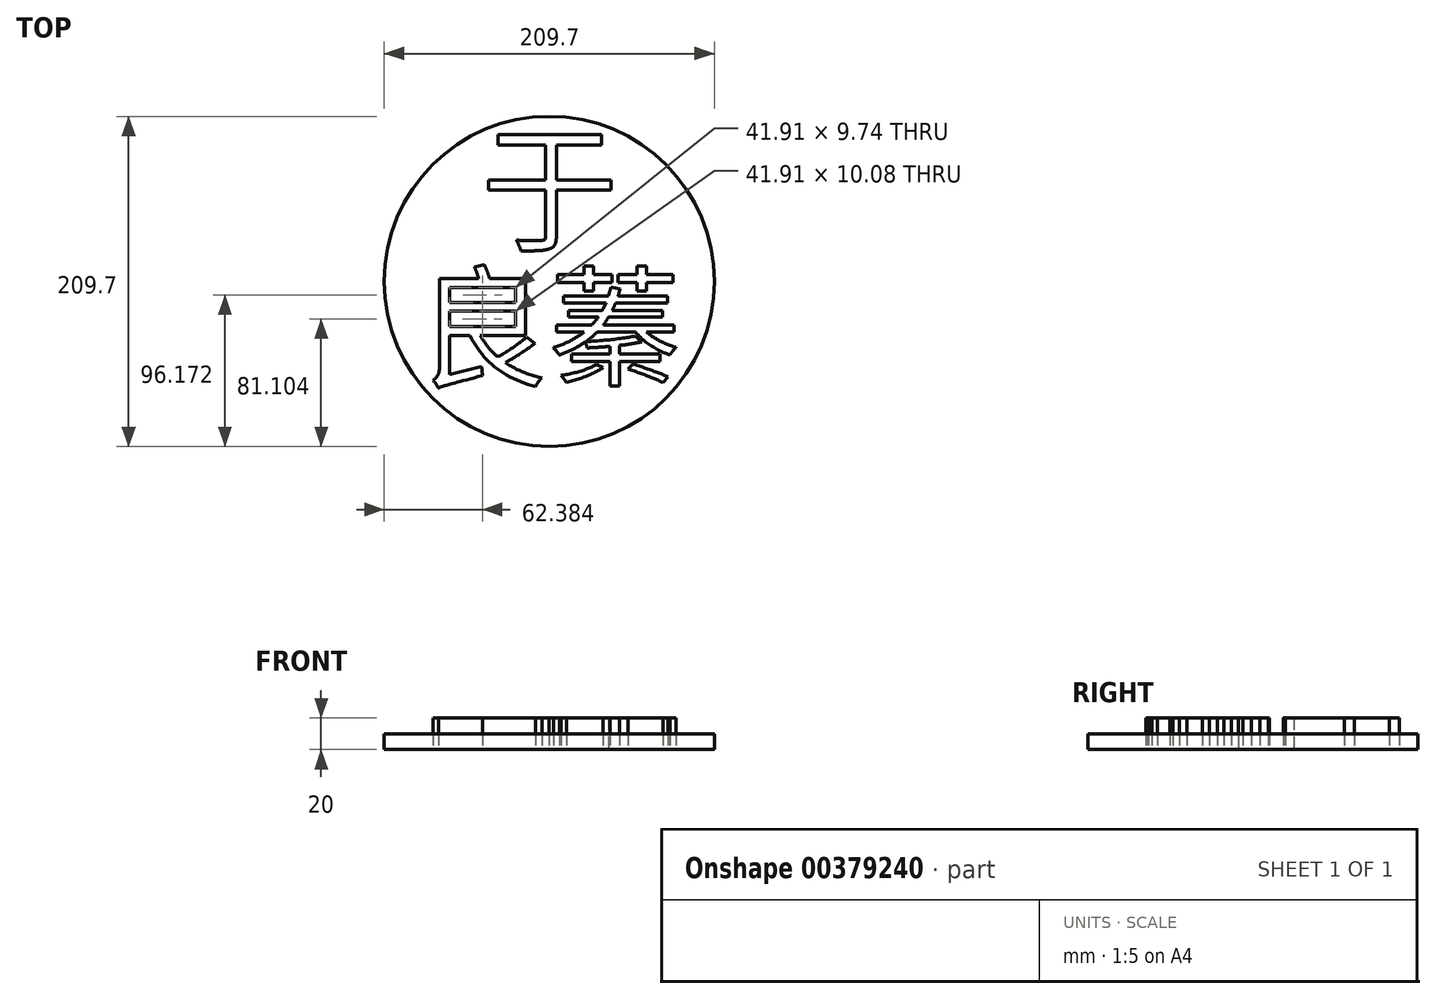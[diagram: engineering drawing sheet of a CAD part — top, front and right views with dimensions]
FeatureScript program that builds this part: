
annotation { "Feature Type Name" : "Feature", "Feature Type Description" : "" }
export const myFeature = defineFeature(function(context is Context, id is Id, definition is map)
    precondition{}
    {
        {
            var Q0;
            Q0=qCreatedBy(makeId("Top.planeOp"),FACE);
            var sketch = newSketch(context, id + "F0", { "sketchPlane" : qUnion([Q0])});
            skCircle(sketch, "E0", {"center": v(0, 0) * mm, "radius": 104.85 * mm});
            skSolve(sketch);
        }
        {
            var Q0;
            Q0=makeQuery(id+"F0.imprint","IMPRINT",FACE,{"disambiguationData":[TD([[makeQuery(id+"F0.imprint","IMPRINT",EDGE,{"derivedFrom":sQuery(id+"F0.wireOp",EDGE,"E0")}),1.0]])]});
            var sketch = newSketch(context, id + "F1", { "sketchPlane" : qUnion([Q0])});
            skText(sketch, "E1", { "text": "于", "fontName": "NotoSansCJKtc-Regular.otf"});
            skText(sketch, "E2", { "text": "良", "fontName": "NotoSansCJKtc-Regular.otf"});
            skText(sketch, "E3", { "text": "蓁", "fontName": "NotoSansCJKtc-Regular.otf"});
            const initialGuessF1  = {"E1": [-0.04386, 0.02571, 1, 0, 0.0635], "E2": [-0.08509, -0.06096, 1, 0, 0.06096], "E3": [0, -0.06018, 1, 0, 0.06018]};
            skSetInitialGuess(sketch, initialGuessF1);
            skSolve(sketch);
        }
        {
            var Q0;
            Q0 = qSketchRegion(id + "F1", true);
            extrude(context, id + "F2", {"entities" : qUnion([Q0]), "depth" : 20 * mm});
        }
        {
            var Q0;
            Q0=makeQuery(id+"F0.imprint","IMPRINT",FACE,{"disambiguationData":[TD([[makeQuery(id+"F0.imprint","IMPRINT",EDGE,{"derivedFrom":sQuery(id+"F0.wireOp",EDGE,"E0")}),1.0]])]});
            extrude(context, id + "F3", {"entities" : qUnion([Q0]), "depth" : 10 * mm});
        }
    });
